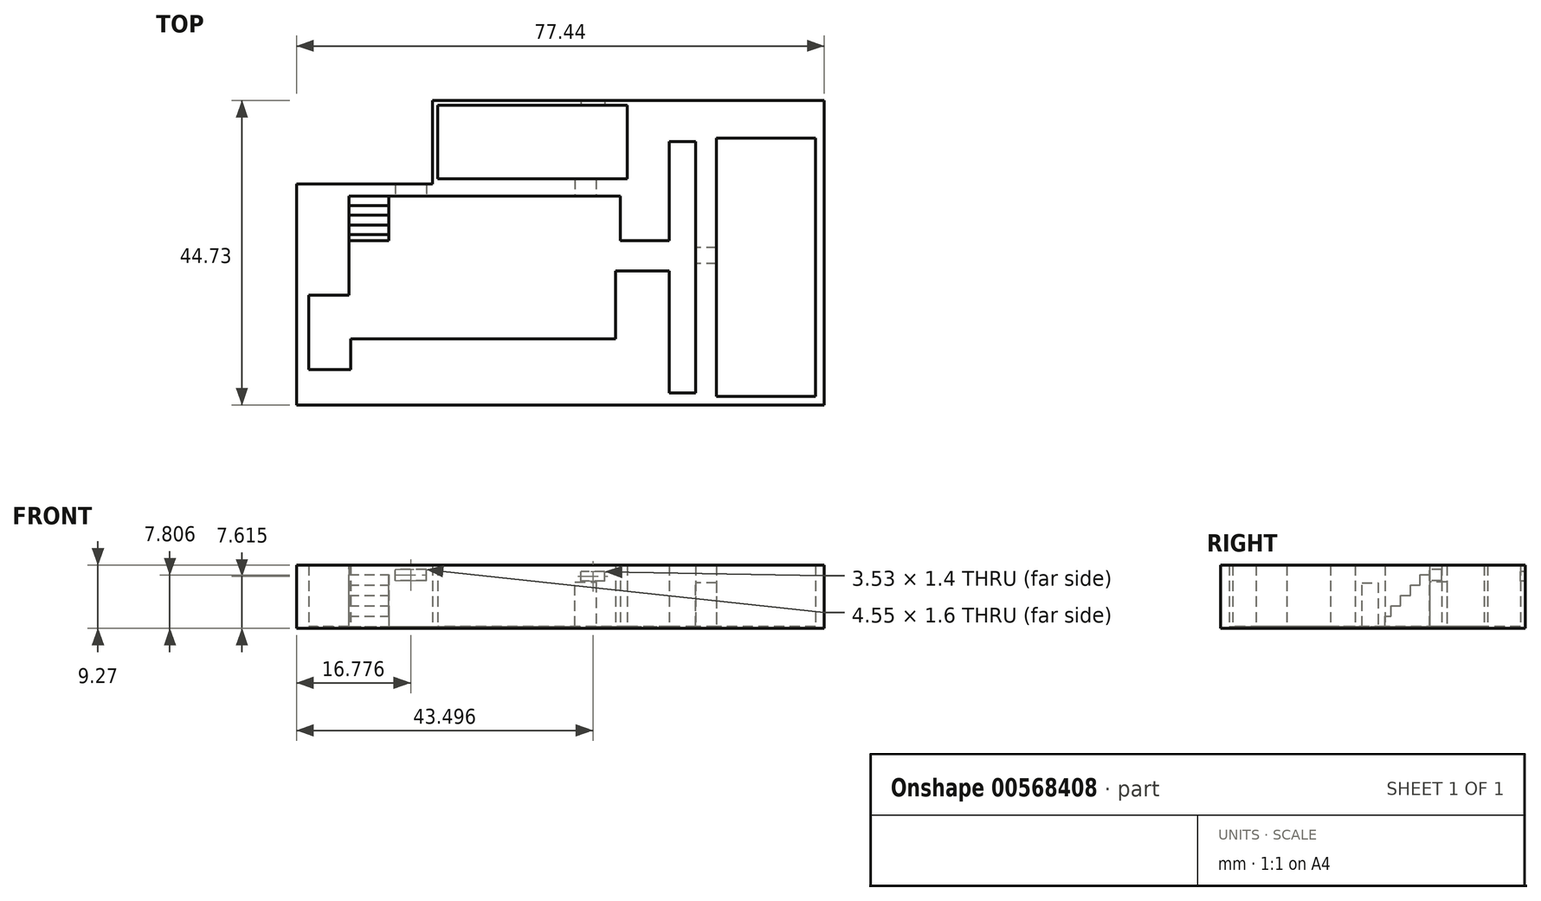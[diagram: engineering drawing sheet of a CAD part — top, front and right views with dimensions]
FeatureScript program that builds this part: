
annotation { "Feature Type Name" : "Feature", "Feature Type Description" : "" }
export const myFeature = defineFeature(function(context is Context, id is Id, definition is map)
    precondition{}
    {
        {
            var Q0;
            Q0=qCreatedBy(makeId("Top.planeOp"),FACE);
            var sketch = newSketch(context, id + "F0", { "sketchPlane" : qUnion([Q0])});
            skLineSegment(sketch, "E0", {"start": v(-54.46, 51.38) * mm, "end": v(-54.46, 36.85) * mm});
            skLineSegment(sketch, "E1", {"start": v(-54.46, 36.85) * mm, "end": v(-60.36, 36.85) * mm});
            skLineSegment(sketch, "E2", {"start": v(-60.36, 36.85) * mm, "end": v(-60.36, 22.31) * mm});
            skLineSegment(sketch, "E3", {"start": v(-60.36, 22.31) * mm, "end": v(-50.6, 22.31) * mm});
            skLineSegment(sketch, "E4", {"start": v(-50.6, 22.31) * mm, "end": v(-50.6, 26.85) * mm});
            skLineSegment(sketch, "E5", {"start": v(-50.6, 26.85) * mm, "end": v(-11.76, 26.85) * mm});
            skLineSegment(sketch, "E6", {"start": v(-11.76, 26.85) * mm, "end": v(-11.76, 36.85) * mm});
            skLineSegment(sketch, "E7", {"start": v(-11.76, 36.85) * mm, "end": v(-7.45, 36.85) * mm});
            skLineSegment(sketch, "E8", {"start": v(-7.45, 36.85) * mm, "end": v(-7.45, 18.9) * mm});
            skLineSegment(sketch, "E9", {"start": v(-7.45, 18.9) * mm, "end": v(0, 18.9) * mm});
            skLineSegment(sketch, "E10", {"start": v(0, 18.9) * mm, "end": v(0, 36.85) * mm});
            skLineSegment(sketch, "E11", {"start": v(0, 42.07) * mm, "end": v(0, 59.33) * mm});
            skLineSegment(sketch, "E12", {"start": v(0, 59.33) * mm, "end": v(-7.45, 59.33) * mm});
            skLineSegment(sketch, "E13", {"start": v(-7.45, 59.33) * mm, "end": v(-7.45, 44.8) * mm});
            skLineSegment(sketch, "E14", {"start": v(-7.45, 44.8) * mm, "end": v(-11.08, 44.8) * mm});
            skLineSegment(sketch, "E15", {"start": v(-11.08, 44.8) * mm, "end": v(-11.08, 51.38) * mm});
            skLineSegment(sketch, "E16", {"start": v(-11.08, 63.64) * mm, "end": v(-40.38, 63.64) * mm});
            skLineSegment(sketch, "E17", {"start": v(-40.38, 63.64) * mm, "end": v(-40.38, 51.38) * mm});
            skLineSegment(sketch, "E18", {"start": v(-40.38, 51.38) * mm, "end": v(-17.44, 51.38) * mm});
            skLineSegment(sketch, "E19", {"start": v(-40.38, 51.38) * mm, "end": v(-49, 51.38) * mm});
            skLineSegment(sketch, "E20", {"start": v(0, 18.9) * mm, "end": v(17.08, 18.9) * mm});
            skLineSegment(sketch, "E21", {"start": v(17.08, 18.9) * mm, "end": v(17.08, 59.33) * mm});
            skLineSegment(sketch, "E22", {"start": v(17.08, 59.33) * mm, "end": v(0, 59.33) * mm});
            skLineSegment(sketch, "E23", {"start": v(-54.46, 51.38) * mm, "end": v(-49, 51.38) * mm});
            skLineSegment(sketch, "E24", {"start": v(-17.44, 51.38) * mm, "end": v(-11.08, 51.38) * mm});
            skLineSegment(sketch, "E25", {"start": v(0, 42.07) * mm, "end": v(0, 36.85) * mm});
            skLineSegment(sketch, "E26.0", {"start": v(-52.68, 49.6) * mm, "end": v(-49, 49.6) * mm});
            skLineSegment(sketch, "E26.1", {"start": v(-40.38, 49.6) * mm, "end": v(-49, 49.6) * mm});
            skLineSegment(sketch, "E26.2", {"start": v(-40.38, 49.6) * mm, "end": v(-17.44, 49.6) * mm});
            skLineSegment(sketch, "E26.3", {"start": v(-17.44, 49.6) * mm, "end": v(-12.86, 49.6) * mm});
            skLineSegment(sketch, "E26.4", {"start": v(-12.86, 43.02) * mm, "end": v(-12.86, 49.6) * mm});
            skLineSegment(sketch, "E26.5", {"start": v(-52.68, 49.6) * mm, "end": v(-52.68, 35.07) * mm});
            skLineSegment(sketch, "E26.6", {"start": v(-5.67, 43.02) * mm, "end": v(-12.86, 43.02) * mm});
            skLineSegment(sketch, "E26.7", {"start": v(-5.67, 57.55) * mm, "end": v(-5.67, 43.02) * mm});
            skLineSegment(sketch, "E26.8", {"start": v(-1.78, 57.55) * mm, "end": v(-5.67, 57.55) * mm});
            skLineSegment(sketch, "E26.9", {"start": v(-1.78, 42.07) * mm, "end": v(-1.78, 57.55) * mm});
            skLineSegment(sketch, "E26.10", {"start": v(-1.78, 42.07) * mm, "end": v(-1.78, 36.85) * mm});
            skLineSegment(sketch, "E26.11", {"start": v(-52.37, 24.1) * mm, "end": v(-52.37, 28.63) * mm});
            skLineSegment(sketch, "E26.12", {"start": v(-58.58, 24.1) * mm, "end": v(-52.37, 24.1) * mm});
            skLineSegment(sketch, "E26.13", {"start": v(-58.58, 35.07) * mm, "end": v(-58.58, 24.1) * mm});
            skLineSegment(sketch, "E26.14", {"start": v(-52.68, 35.07) * mm, "end": v(-58.58, 35.07) * mm});
            skLineSegment(sketch, "E26.15", {"start": v(-52.37, 28.63) * mm, "end": v(-13.54, 28.63) * mm});
            skLineSegment(sketch, "E26.16", {"start": v(-13.54, 28.63) * mm, "end": v(-13.54, 38.62) * mm});
            skLineSegment(sketch, "E26.17", {"start": v(-13.54, 38.62) * mm, "end": v(-5.67, 38.62) * mm});
            skLineSegment(sketch, "E26.18", {"start": v(-5.67, 38.62) * mm, "end": v(-5.67, 20.68) * mm});
            skLineSegment(sketch, "E26.19", {"start": v(-5.67, 20.68) * mm, "end": v(-1.78, 20.68) * mm});
            skLineSegment(sketch, "E26.20", {"start": v(-1.78, 20.68) * mm, "end": v(-1.78, 36.85) * mm});
            skLineSegment(sketch, "E27.0", {"start": v(1.27, 42.07) * mm, "end": v(1.27, 36.85) * mm});
            skLineSegment(sketch, "E27.1", {"start": v(15.8, 58.06) * mm, "end": v(1.27, 58.06) * mm});
            skLineSegment(sketch, "E27.2", {"start": v(15.8, 20.18) * mm, "end": v(15.8, 58.06) * mm});
            skLineSegment(sketch, "E27.3", {"start": v(1.27, 42.07) * mm, "end": v(1.27, 58.06) * mm});
            skLineSegment(sketch, "E27.4", {"start": v(1.27, 20.18) * mm, "end": v(15.8, 20.18) * mm});
            skLineSegment(sketch, "E27.5", {"start": v(1.27, 20.18) * mm, "end": v(1.27, 36.85) * mm});
            skLineSegment(sketch, "E28", {"start": v(-11.08, 63.64) * mm, "end": v(-11.08, 51.38) * mm});
            skLineSegment(sketch, "E29.0", {"start": v(-17.44, 52.12) * mm, "end": v(-11.82, 52.12) * mm});
            skLineSegment(sketch, "E29.1", {"start": v(-11.82, 62.9) * mm, "end": v(-11.82, 52.12) * mm});
            skLineSegment(sketch, "E29.2", {"start": v(-39.64, 52.12) * mm, "end": v(-17.44, 52.12) * mm});
            skLineSegment(sketch, "E29.3", {"start": v(-39.64, 62.9) * mm, "end": v(-39.64, 52.12) * mm});
            skLineSegment(sketch, "E29.4", {"start": v(-11.82, 62.9) * mm, "end": v(-39.64, 62.9) * mm});
            skSolve(sketch);
        }
        {
            var Q0;
            Q0=makeQuery(id+"F0.imprint","IMPRINT",FACE,{"disambiguationData":[TD([[makeQuery(id+"F0.imprint","IMPRINT",EDGE,{"derivedFrom":sQuery(id+"F0.wireOp",EDGE,"E0")}),1.0]])]});
            var Q1;
            Q1=makeQuery(id+"F0.imprint","IMPRINT",FACE,{"disambiguationData":[TD([[makeQuery(id+"F0.imprint","IMPRINT",EDGE,{"derivedFrom":sQuery(id+"F0.wireOp",EDGE,"E10")}),-1.0]])]});
            var Q2;
            {var subQ0=sQuery(id+"F0.wireOp",EDGE,"E16");Q2=makeQuery(id+"F0.imprint","IMPRINT",FACE,{"disambiguationData":[TD([[makeQuery(id+"F0.imprint","IMPRINT",EDGE,{"derivedFrom":subQ0}),1.0]])]});}
            extrude(context, id + "F1", {"entities" : qUnion([Q0, Q1, Q2]), "depth" : 9.27 * mm, "offsetDistance" : 25.4 * mm});
        }
        {
            var Q0;
            Q0=makeQuery(id+"F0.imprint","IMPRINT",FACE,{"disambiguationData":[TD([[makeQuery(id+"F0.imprint","IMPRINT",EDGE,{"derivedFrom":sQuery(id+"F0.wireOp",EDGE,"E26.0")}),-1.0]])]});
            var Q1;
            Q1=makeQuery(id+"F0.imprint","IMPRINT",FACE,{"disambiguationData":[TD([[makeQuery(id+"F0.imprint","IMPRINT",EDGE,{"derivedFrom":sQuery(id+"F0.wireOp",EDGE,"E27.0")}),1.0]])]});
            var Q2;
            Q2=makeQuery(id+"F0.imprint","IMPRINT",FACE,{"disambiguationData":[TD([[makeQuery(id+"F0.imprint","IMPRINT",EDGE,{"derivedFrom":sQuery(id+"F0.wireOp",EDGE,"E29.0")}),1.0]])]});
            extrude(context, id + "F2", {"entities" : qUnion([Q0, Q1, Q2]), "operationType" : NewBodyOperationType.ADD, "depth" : 0.25 * mm, "offsetDistance" : 25.4 * mm});
        }
        {
            var Q0;
            Q0=makeQuery(id+"F1.opExtrude","SWEPT_FACE",FACE,{"disambiguationData":[OSD([sQuery(id+"F0.wireOp",EDGE,"E26.0"),sQuery(id+"F0.wireOp",EDGE,"E26.1"),sQuery(id+"F0.wireOp",EDGE,"E26.2"),sQuery(id+"F0.wireOp",EDGE,"E26.3")])]});
            var sketch = newSketch(context, id + "F3", { "sketchPlane" : qUnion([Q0])});
            skLineSegment(sketch, "E30", {"start": v(-19.48, 0.25) * mm, "end": v(-19.48, 6.78) * mm});
            skLineSegment(sketch, "E31", {"start": v(-19.48, 6.78) * mm, "end": v(-16.42, 6.78) * mm});
            skLineSegment(sketch, "E32", {"start": v(-16.42, 6.78) * mm, "end": v(-16.42, 0.25) * mm});
            skSolve(sketch);
        }
        {
            var Q0;
            Q0 = qSketchRegion(id + "F3", true);
            var Q1;
            {var subQ0=sQuery(id+"F3.wireOp",EDGE,"E30");Q1=makeQuery(id+"F3.imprint","IMPRINT",FACE,{"disambiguationData":[TD([[makeQuery(id+"F3.imprint","IMPRINT",EDGE,{"derivedFrom":subQ0}),-1.0]])]});}
            extrude(context, id + "F4", {"entities" : qUnion([Q0, Q1]), "operationType" : NewBodyOperationType.REMOVE, "oppositeDirection" : true, "depth" : 8.38 * mm, "offsetDistance" : 25.4 * mm});
        }
        {
            var Q0;
            Q0=makeQuery(id+"F1.opExtrude","SWEPT_FACE",FACE,{"disambiguationData":[OSD([sQuery(id+"F0.wireOp",EDGE,"E26.9"),sQuery(id+"F0.wireOp",EDGE,"E26.10"),sQuery(id+"F0.wireOp",EDGE,"E26.20")])]});
            var sketch = newSketch(context, id + "F5", { "sketchPlane" : qUnion([Q0])});
            skLineSegment(sketch, "E33", {"start": v(-42, 0.25) * mm, "end": v(-42, 6.7) * mm});
            skLineSegment(sketch, "E34", {"start": v(-42, 6.7) * mm, "end": v(-39.65, 6.7) * mm});
            skLineSegment(sketch, "E35", {"start": v(-39.65, 6.7) * mm, "end": v(-39.65, 0.25) * mm});
            skSolve(sketch);
        }
        {
            var Q0;
            Q0 = qSketchRegion(id + "F5", true);
            var Q1;
            {var subQ0=sQuery(id+"F5.wireOp",EDGE,"E33");Q1=makeQuery(id+"F5.imprint","IMPRINT",FACE,{"disambiguationData":[TD([[makeQuery(id+"F5.imprint","IMPRINT",EDGE,{"derivedFrom":subQ0}),-1.0]])]});}
            extrude(context, id + "F6", {"entities" : qUnion([Q0, Q1]), "operationType" : NewBodyOperationType.REMOVE, "oppositeDirection" : true, "depth" : 12.45 * mm, "offsetDistance" : 25.4 * mm});
        }
        {
            var Q0;
            {var subQ0=sQuery(id+"F0.wireOp",EDGE,"E26.20");var subQ1=sQuery(id+"F0.wireOp",EDGE,"E26.10");var subQ2=sQuery(id+"F0.wireOp",EDGE,"E26.9");var subQ3=sQuery(id+"F0.wireOp",EDGE,"E26.3");var subQ4=sQuery(id+"F0.wireOp",EDGE,"E26.2");var subQ5=sQuery(id+"F0.wireOp",EDGE,"E26.1");var subQ6=sQuery(id+"F0.wireOp",EDGE,"E26.0");Q0=makeQuery(id+"F6.boolean.opBoolean","MERGE",FACE,{"derivedFrom":[makeQuery(id+"F2.opExtrude","CAP_FACE",FACE,{"disambiguationData":[OSD([sQuery(id+"F0.wireOp",EDGE,"E27.0"),sQuery(id+"F0.wireOp",EDGE,"E27.1"),sQuery(id+"F0.wireOp",EDGE,"E27.2"),sQuery(id+"F0.wireOp",EDGE,"E27.3"),sQuery(id+"F0.wireOp",EDGE,"E27.4"),sQuery(id+"F0.wireOp",EDGE,"E27.5")])],"isStart":false}),makeQuery(id+"F4.boolean.opBoolean","MERGE",FACE,{"derivedFrom":[makeQuery(id+"F2.opExtrude","CAP_FACE",FACE,{"disambiguationData":[OSD([subQ6,subQ5,subQ4,subQ3,sQuery(id+"F0.wireOp",EDGE,"E26.4"),sQuery(id+"F0.wireOp",EDGE,"E26.5"),sQuery(id+"F0.wireOp",EDGE,"E26.6"),sQuery(id+"F0.wireOp",EDGE,"E26.7"),sQuery(id+"F0.wireOp",EDGE,"E26.8"),subQ2,subQ1,sQuery(id+"F0.wireOp",EDGE,"E26.11"),sQuery(id+"F0.wireOp",EDGE,"E26.12"),sQuery(id+"F0.wireOp",EDGE,"E26.13"),sQuery(id+"F0.wireOp",EDGE,"E26.14"),sQuery(id+"F0.wireOp",EDGE,"E26.15"),sQuery(id+"F0.wireOp",EDGE,"E26.16"),sQuery(id+"F0.wireOp",EDGE,"E26.17"),sQuery(id+"F0.wireOp",EDGE,"E26.18"),sQuery(id+"F0.wireOp",EDGE,"E26.19"),subQ0])],"isStart":false}),makeQuery(id+"F2.opExtrude","CAP_FACE",FACE,{"disambiguationData":[OSD([sQuery(id+"F0.wireOp",EDGE,"E29.0"),sQuery(id+"F0.wireOp",EDGE,"E29.1"),sQuery(id+"F0.wireOp",EDGE,"E29.2"),sQuery(id+"F0.wireOp",EDGE,"E29.3"),sQuery(id+"F0.wireOp",EDGE,"E29.4")])],"isStart":false}),makeQuery(id+"F4.opExtrude","SWEPT_FACE",FACE,{"disambiguationData":[OSD([subQ6,subQ5,subQ4,subQ3])]})]}),makeQuery(id+"F6.opExtrude","SWEPT_FACE",FACE,{"disambiguationData":[OSD([subQ2,subQ1,subQ0])]})]});}
            var sketch = newSketch(context, id + "F7", { "sketchPlane" : qUnion([Q0])});
            skLineSegment(sketch, "E36", {"start": v(-52.68, 49.6) * mm, "end": v(-52.68, 43.02) * mm});
            skLineSegment(sketch, "E37", {"start": v(-52.68, 43.02) * mm, "end": v(-46.8, 43.02) * mm});
            skLineSegment(sketch, "E38", {"start": v(-46.8, 43.02) * mm, "end": v(-46.8, 49.6) * mm});
            skSolve(sketch);
        }
        {
            var Q0;
            Q0 = qSketchRegion(id + "F7", true);
            var Q1;
            {var subQ0=sQuery(id+"F7.wireOp",EDGE,"E36");Q1=makeQuery(id+"F7.imprint","IMPRINT",FACE,{"disambiguationData":[TD([[makeQuery(id+"F7.imprint","IMPRINT",EDGE,{"derivedFrom":subQ0}),1.0]])]});}
            extrude(context, id + "F8", {"entities" : qUnion([Q0, Q1]), "operationType" : NewBodyOperationType.ADD, "depth" : 9.02 * mm, "offsetDistance" : 25.4 * mm});
        }
        {
            var Q0;
            Q0=makeQuery(id+"F8.opExtrude","SWEPT_FACE",FACE,{"disambiguationData":[OSD([sQuery(id+"F7.wireOp",EDGE,"E38")])]});
            var sketch = newSketch(context, id + "F9", { "sketchPlane" : qUnion([Q0])});
            skLineSegment(sketch, "E39", {"start": v(43.02, 0.25) * mm, "end": v(43.02, 1.78) * mm});
            skLineSegment(sketch, "E40", {"start": v(43.02, 1.78) * mm, "end": v(43.91, 1.78) * mm});
            skLineSegment(sketch, "E41", {"start": v(43.91, 1.78) * mm, "end": v(43.91, 3.3) * mm});
            skLineSegment(sketch, "E42", {"start": v(43.91, 3.3) * mm, "end": v(45.33, 3.3) * mm});
            skLineSegment(sketch, "E43", {"start": v(45.33, 3.3) * mm, "end": v(45.33, 4.83) * mm});
            skLineSegment(sketch, "E44", {"start": v(45.33, 4.83) * mm, "end": v(46.76, 4.83) * mm});
            skLineSegment(sketch, "E45", {"start": v(46.76, 4.83) * mm, "end": v(46.76, 6.35) * mm});
            skLineSegment(sketch, "E46", {"start": v(46.76, 6.35) * mm, "end": v(48.18, 6.35) * mm});
            skLineSegment(sketch, "E47", {"start": v(48.18, 6.35) * mm, "end": v(48.18, 7.87) * mm});
            skLineSegment(sketch, "E48", {"start": v(48.18, 7.87) * mm, "end": v(49.6, 7.87) * mm});
            skSolve(sketch);
        }
        {
            var Q0;
            Q0 = qSketchRegion(id + "F9", true);
            var Q1;
            {var subQ3=sQuery(id+"F9.wireOp",EDGE,"E40");Q1=makeQuery(id+"F9.imprint","IMPRINT",FACE,{"disambiguationData":[TD([[makeQuery(id+"F9.imprint","IMPRINT",EDGE,{"derivedFrom":subQ3}),1.0]])]});}
            extrude(context, id + "F10", {"entities" : qUnion([Q0, Q1]), "operationType" : NewBodyOperationType.REMOVE, "oppositeDirection" : true, "depth" : 5.87 * mm, "offsetDistance" : 25.4 * mm});
        }
        {
            var Q0;
            {var subQ0=sQuery(id+"F0.wireOp",EDGE,"E26.3");var subQ1=sQuery(id+"F0.wireOp",EDGE,"E26.2");var subQ2=sQuery(id+"F0.wireOp",EDGE,"E26.1");var subQ3=sQuery(id+"F0.wireOp",EDGE,"E26.0");Q0=makeQuery(id+"F10.boolean.opBoolean","MERGE",FACE,{"derivedFrom":[makeQuery(id+"F1.opExtrude","SWEPT_FACE",FACE,{"disambiguationData":[OSD([subQ3,subQ2,subQ1,subQ0])]}),makeQuery(id+"F10.opExtrude","SWEPT_FACE",FACE,{"disambiguationData":[OSD([subQ3,subQ2,subQ1,subQ0,sQuery(id+"F7.wireOp",EDGE,"E38")])]})]});}
            var sketch = newSketch(context, id + "F11", { "sketchPlane" : qUnion([Q0])});
            skLineSegment(sketch, "E49.bottom", {"start": v(-41.3, 7) * mm, "end": v(-45.86, 7) * mm});
            skLineSegment(sketch, "E49.top", {"start": v(-41.3, 8.6) * mm, "end": v(-45.86, 8.6) * mm});
            skLineSegment(sketch, "E49.left", {"start": v(-41.3, 7) * mm, "end": v(-41.3, 8.6) * mm});
            skLineSegment(sketch, "E49.right", {"start": v(-45.86, 7) * mm, "end": v(-45.86, 8.6) * mm});
            skPoint(sketch, "E49.middle", {"position": v(-43.58, 7.8) * mm});
            skSolve(sketch);
        }
        {
            var Q0;
            Q0 = qSketchRegion(id + "F11", true);
            extrude(context, id + "F12", {"entities" : qUnion([Q0]), "operationType" : NewBodyOperationType.REMOVE, "oppositeDirection" : true, "depth" : 25.4 * mm, "offsetDistance" : 25.4 * mm});
        }
        {
            var Q0;
            Q0=makeQuery(id+"F1.opExtrude","SWEPT_FACE",FACE,{"disambiguationData":[OSD([sQuery(id+"F0.wireOp",EDGE,"E29.4")])]});
            var sketch = newSketch(context, id + "F13", { "sketchPlane" : qUnion([Q0])});
            skLineSegment(sketch, "E50.bottom", {"start": v(-15.1, 6.91) * mm, "end": v(-18.63, 6.91) * mm});
            skLineSegment(sketch, "E50.top", {"start": v(-15.1, 8.32) * mm, "end": v(-18.63, 8.32) * mm});
            skLineSegment(sketch, "E50.left", {"start": v(-15.1, 6.91) * mm, "end": v(-15.1, 8.32) * mm});
            skLineSegment(sketch, "E50.right", {"start": v(-18.63, 6.91) * mm, "end": v(-18.63, 8.32) * mm});
            skPoint(sketch, "E50.middle", {"position": v(-16.86, 7.61) * mm});
            skSolve(sketch);
        }
        {
            var Q0;
            Q0 = qSketchRegion(id + "F13", true);
            extrude(context, id + "F14", {"entities" : qUnion([Q0]), "operationType" : NewBodyOperationType.REMOVE, "oppositeDirection" : true, "depth" : 25.4 * mm, "offsetDistance" : 25.4 * mm});
        }
        {
            var Q0;
            Q0=makeQuery(id+"F1.opExtrude","SWEPT_FACE",FACE,{"disambiguationData":[OSD([sQuery(id+"F0.wireOp",EDGE,"E0")])]});
            var sketch = newSketch(context, id + "F15", { "sketchPlane" : qUnion([Q0])});
            skLineSegment(sketch, "E51", {"start": v(-51.38, 9.27) * mm, "end": v(-36.85, 9.27) * mm});
            skLineSegment(sketch, "E52", {"start": v(-36.85, 9.27) * mm, "end": v(-36.85, 0) * mm});
            skLineSegment(sketch, "E53", {"start": v(-36.85, 0) * mm, "end": v(-51.38, 0) * mm});
            skLineSegment(sketch, "E54", {"start": v(-51.38, 0) * mm, "end": v(-51.38, 9.27) * mm});
            skSolve(sketch);
        }
        {
            var Q0;
            Q0 = qSketchRegion(id + "F15", true);
            extrude(context, id + "F16", {"entities" : qUnion([Q0]), "operationType" : NewBodyOperationType.ADD, "depth" : 5.9 * mm, "offsetDistance" : 25.4 * mm});
        }
        {
            var Q0;
            Q0=makeQuery(id+"F1.opExtrude","SWEPT_FACE",FACE,{"disambiguationData":[OSD([sQuery(id+"F0.wireOp",EDGE,"E4")])]});
            var sketch = newSketch(context, id + "F17", { "sketchPlane" : qUnion([Q0])});
            skLineSegment(sketch, "E55", {"start": v(22.31, 9.27) * mm, "end": v(22.31, 0) * mm});
            skLineSegment(sketch, "E56", {"start": v(22.31, 0) * mm, "end": v(26.85, 0) * mm});
            skLineSegment(sketch, "E57", {"start": v(26.85, 0) * mm, "end": v(26.85, 9.27) * mm});
            skLineSegment(sketch, "E58", {"start": v(26.85, 9.27) * mm, "end": v(22.31, 9.27) * mm});
            skSolve(sketch);
        }
        {
            var Q0;
            Q0 = qSketchRegion(id + "F17", true);
            extrude(context, id + "F18", {"entities" : qUnion([Q0]), "operationType" : NewBodyOperationType.ADD, "depth" : 43.46 * mm, "offsetDistance" : 25.4 * mm});
        }
        {
            var Q0;
            Q0=makeQuery(id+"F1.opExtrude","SWEPT_FACE",FACE,{"disambiguationData":[OSD([sQuery(id+"F0.wireOp",EDGE,"E7")])]});
            var sketch = newSketch(context, id + "F19", { "sketchPlane" : qUnion([Q0])});
            skLineSegment(sketch, "E59", {"start": v(-11.76, 9.27) * mm, "end": v(-11.76, 0) * mm});
            skLineSegment(sketch, "E60", {"start": v(-11.76, 0) * mm, "end": v(-7.45, 0) * mm});
            skLineSegment(sketch, "E61", {"start": v(-7.45, 0) * mm, "end": v(-7.45, 9.27) * mm});
            skLineSegment(sketch, "E62", {"start": v(-7.45, 9.27) * mm, "end": v(-11.76, 9.27) * mm});
            skSolve(sketch);
        }
        {
            var Q0;
            Q0 = qSketchRegion(id + "F19", true);
            extrude(context, id + "F20", {"entities" : qUnion([Q0]), "operationType" : NewBodyOperationType.ADD, "depth" : 12.42 * mm, "offsetDistance" : 25.4 * mm});
        }
        {
            var Q0;
            {var subQ45=sQuery(id+"F0.wireOp",EDGE,"E8");var subQ50=sQuery(id+"F0.wireOp",EDGE,"E3");Q0=makeQuery(id+"F18.boolean.opBoolean","SPLIT",FACE,{"disambiguationData":[TD([makeQuery(id+"F1.opExtrude","SWEPT_FACE",FACE,{"disambiguationData":[OSD([subQ50])]})])],"derivedFrom":makeQuery(id+"F1.opExtrude","SWEPT_FACE",FACE,{"disambiguationData":[OSD([subQ45])]})});}
            var sketch = newSketch(context, id + "F21", { "sketchPlane" : qUnion([Q0])});
            skLineSegment(sketch, "E63", {"start": v(-18.9, 9.27) * mm, "end": v(-18.9, 0) * mm});
            skLineSegment(sketch, "E64", {"start": v(-18.9, 0) * mm, "end": v(-22.31, 0) * mm});
            skLineSegment(sketch, "E65", {"start": v(-22.31, 0) * mm, "end": v(-22.31, 9.27) * mm});
            skLineSegment(sketch, "E66", {"start": v(-22.31, 9.27) * mm, "end": v(-18.9, 9.27) * mm});
            skSolve(sketch);
        }
        {
            var Q0;
            Q0 = qSketchRegion(id + "F21", true);
            extrude(context, id + "F22", {"entities" : qUnion([Q0]), "operationType" : NewBodyOperationType.ADD, "depth" : 52.9 * mm, "offsetDistance" : 25.4 * mm});
        }
        {
            var Q0;
            Q0=makeQuery(id+"F1.opExtrude","SWEPT_FACE",FACE,{"disambiguationData":[OSD([sQuery(id+"F0.wireOp",EDGE,"E14")])]});
            var sketch = newSketch(context, id + "F23", { "sketchPlane" : qUnion([Q0])});
            skLineSegment(sketch, "E67", {"start": v(7.45, 9.27) * mm, "end": v(7.45, 0) * mm});
            skLineSegment(sketch, "E68", {"start": v(7.45, 0) * mm, "end": v(11.08, 0) * mm});
            skLineSegment(sketch, "E69", {"start": v(11.08, 0) * mm, "end": v(11.08, 9.27) * mm});
            skLineSegment(sketch, "E70", {"start": v(11.08, 9.27) * mm, "end": v(7.45, 9.27) * mm});
            skSolve(sketch);
        }
        {
            var Q0;
            Q0 = qSketchRegion(id + "F23", true);
            extrude(context, id + "F24", {"entities" : qUnion([Q0]), "operationType" : NewBodyOperationType.ADD, "depth" : 18.85 * mm, "offsetDistance" : 25.4 * mm});
        }
        {
            var Q0;
            Q0=makeQuery(id+"F24.opExtrude","SWEPT_FACE",FACE,{"disambiguationData":[OSD([sQuery(id+"F23.wireOp",EDGE,"E67")])]});
            var sketch = newSketch(context, id + "F25", { "sketchPlane" : qUnion([Q0])});
            skLineSegment(sketch, "E71", {"start": v(59.33, 9.27) * mm, "end": v(63.64, 9.27) * mm});
            skLineSegment(sketch, "E72", {"start": v(63.64, 9.27) * mm, "end": v(63.64, 0) * mm});
            skLineSegment(sketch, "E73", {"start": v(63.64, 0) * mm, "end": v(59.33, 0) * mm});
            skLineSegment(sketch, "E74", {"start": v(59.33, 0) * mm, "end": v(59.33, 9.27) * mm});
            skSolve(sketch);
        }
        {
            var Q0;
            Q0 = qSketchRegion(id + "F25", true);
            extrude(context, id + "F26", {"entities" : qUnion([Q0]), "operationType" : NewBodyOperationType.ADD, "depth" : 24.52 * mm, "offsetDistance" : 25.4 * mm});
        }
    });
